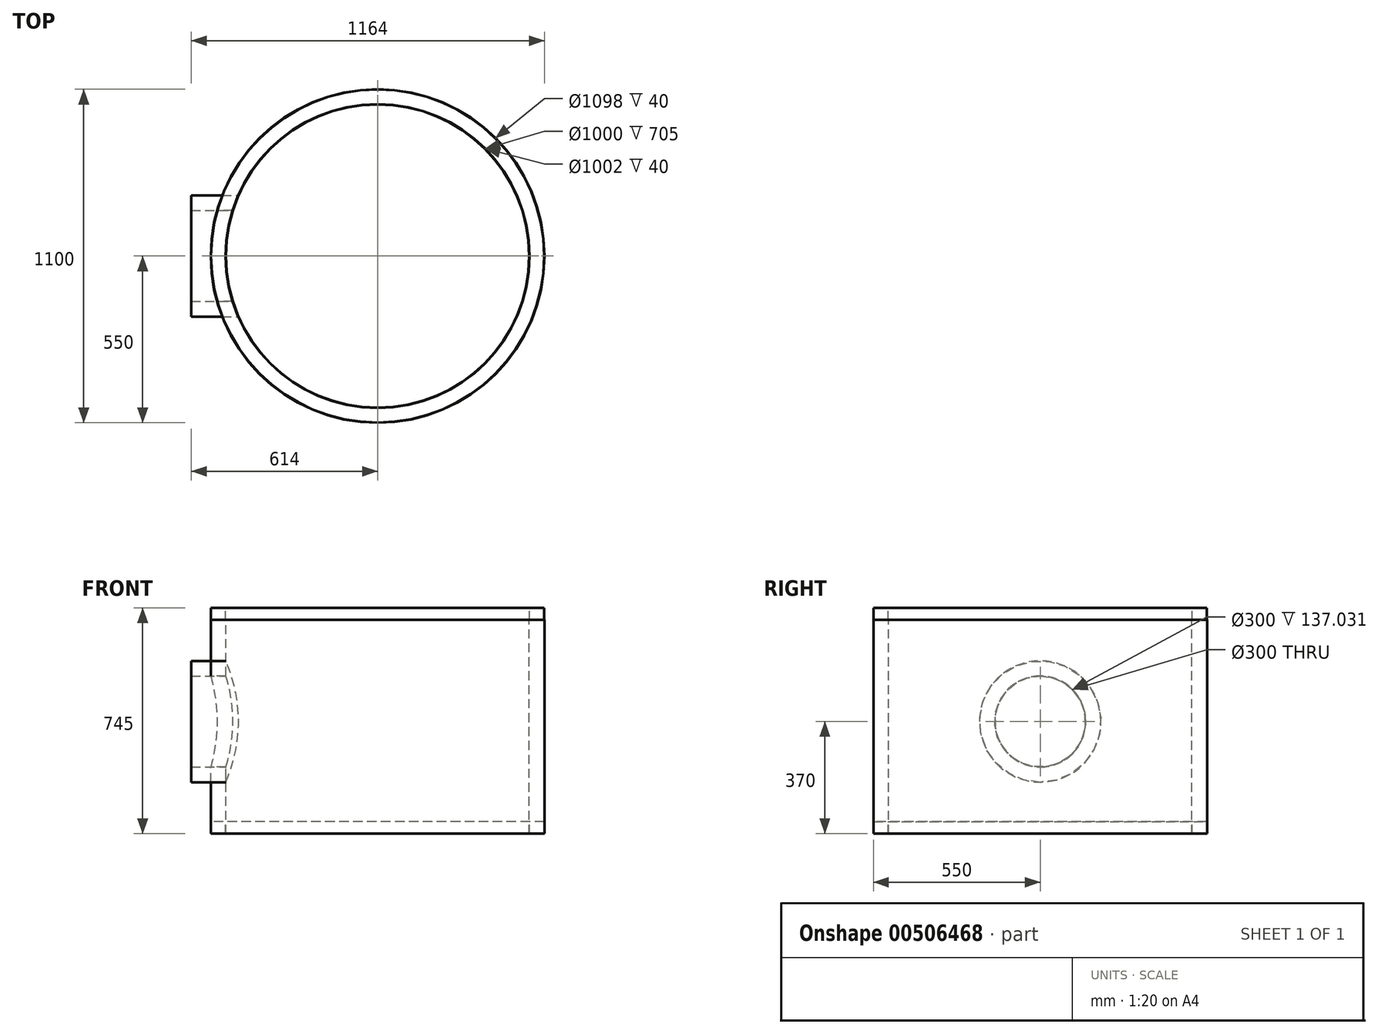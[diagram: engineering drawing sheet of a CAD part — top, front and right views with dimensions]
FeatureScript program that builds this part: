
annotation { "Feature Type Name" : "Feature", "Feature Type Description" : "" }
export const myFeature = defineFeature(function(context is Context, id is Id, definition is map)
    precondition{}
    {
        {
            var Q0;
            Q0=qCreatedBy(makeId("Front.planeOp"),FACE);
            var sketch = newSketch(context, id + "F0", { "sketchPlane" : qUnion([Q0])});
            skLineSegment(sketch, "E0", {"start": v(0, 722.18) * mm, "end": v(0, -793.11) * mm, "construction": true});
            skLineSegment(sketch, "E1", {"start": v(-500, -370) * mm, "end": v(-500, 335) * mm});
            skLineSegment(sketch, "E2", {"start": v(-500, 335) * mm, "end": v(-501, 335) * mm});
            skLineSegment(sketch, "E3", {"start": v(-501, 335) * mm, "end": v(-501, 375) * mm});
            skLineSegment(sketch, "E4", {"start": v(-501, 375) * mm, "end": v(-549, 375) * mm});
            skLineSegment(sketch, "E5", {"start": v(-549, 375) * mm, "end": v(-549, 335) * mm});
            skLineSegment(sketch, "E6", {"start": v(-549, 335) * mm, "end": v(-550, 335) * mm});
            skLineSegment(sketch, "E7", {"start": v(-550, 335) * mm, "end": v(-550, -370) * mm});
            skLineSegment(sketch, "E8", {"start": v(-550, -370) * mm, "end": v(-549, -370) * mm});
            skLineSegment(sketch, "E9", {"start": v(-549, -370) * mm, "end": v(-549, -330) * mm});
            skLineSegment(sketch, "E10", {"start": v(-549, -330) * mm, "end": v(-501, -330) * mm});
            skLineSegment(sketch, "E11", {"start": v(-501, -330) * mm, "end": v(-501, -370) * mm});
            skLineSegment(sketch, "E12", {"start": v(-501, -370) * mm, "end": v(-500, -370) * mm});
            skLineSegment(sketch, "E13", {"start": v(0, 0) * mm, "end": v(-1128, 0) * mm, "construction": true});
            skLineSegment(sketch, "E14", {"start": v(0, -150) * mm, "end": v(-614, -150) * mm});
            skLineSegment(sketch, "E15", {"start": v(-614, -150) * mm, "end": v(-614, -200) * mm});
            skLineSegment(sketch, "E16", {"start": v(-614, -200) * mm, "end": v(0, -200) * mm});
            skLineSegment(sketch, "E17", {"start": v(0, -200) * mm, "end": v(0, -150) * mm});
            skLineSegment(sketch, "E18", {"start": v(-614, -150) * mm, "end": v(-614, 0) * mm});
            skLineSegment(sketch, "E19", {"start": v(-614, 0) * mm, "end": v(-564, 0) * mm});
            skLineSegment(sketch, "E20", {"start": v(-564, 0) * mm, "end": v(-564, -150) * mm});
            skSolve(sketch);
        }
        {
            var Q0;
            {var subQ0=sQuery(id+"F0.wireOp",EDGE,"E2");Q0=makeQuery(id+"F0.imprint","IMPRINT",FACE,{"disambiguationData":[TD([[makeQuery(id+"F0.imprint","IMPRINT",EDGE,{"derivedFrom":subQ0}),1.0]])]});}
            var Q1;
            {var subQ0=sQuery(id+"F0.wireOp",EDGE,"E16");var subQ1=sQuery(id+"F0.wireOp",EDGE,"E1");var subQ2=makeQuery(id+"F0.imprint","INTERSECT",VERTEX,{"derivedFrom":[subQ1,subQ0]});Q1=makeQuery(id+"F0.imprint","IMPRINT",FACE,{"disambiguationData":[TD([[makeQuery(id+"F0.imprint","IMPRINT",EDGE,{"disambiguationData":[TD([[subQ2,-1.0]])],"derivedFrom":subQ1}),1.0]])]});}
            var Q2;
            {var subQ0=sQuery(id+"F0.wireOp",EDGE,"E8");Q2=makeQuery(id+"F0.imprint","IMPRINT",FACE,{"disambiguationData":[TD([[makeQuery(id+"F0.imprint","IMPRINT",EDGE,{"derivedFrom":subQ0}),1.0]])]});}
            var Q3;
            Q3=sQuery(id+"F0.wireOp",EDGE,"E0");
            revolve(context, id + "F1", {"entities" : qUnion([Q0, Q1, Q2]), "axis" : qUnion([Q3]), "revolveType" : RevolveType.FULL});
        }
        {
            var Q0;
            {var subQ0=sQuery(id+"F0.wireOp",EDGE,"E18");Q0=makeQuery(id+"F0.imprint","IMPRINT",FACE,{"disambiguationData":[TD([[makeQuery(id+"F0.imprint","IMPRINT",EDGE,{"derivedFrom":subQ0}),-1.0]])]});}
            var Q1;
            {var subQ0=sQuery(id+"F0.wireOp",EDGE,"E15");Q1=makeQuery(id+"F0.imprint","IMPRINT",FACE,{"disambiguationData":[TD([[makeQuery(id+"F0.imprint","IMPRINT",EDGE,{"derivedFrom":subQ0}),1.0]])]});}
            var Q2;
            {var subQ0=sQuery(id+"F0.wireOp",EDGE,"E16");var subQ1=sQuery(id+"F0.wireOp",EDGE,"E1");var subQ2=makeQuery(id+"F0.imprint","INTERSECT",VERTEX,{"derivedFrom":[subQ1,subQ0]});Q2=makeQuery(id+"F0.imprint","IMPRINT",FACE,{"disambiguationData":[TD([[makeQuery(id+"F0.imprint","IMPRINT",EDGE,{"disambiguationData":[TD([[subQ2,-1.0]])],"derivedFrom":subQ1}),1.0]])]});}
            var Q3;
            {var subQ5=sQuery(id+"F0.wireOp",EDGE,"E17");Q3=makeQuery(id+"F0.imprint","IMPRINT",FACE,{"disambiguationData":[TD([[makeQuery(id+"F0.imprint","IMPRINT",EDGE,{"derivedFrom":subQ5}),1.0]])]});}
            var Q4;
            Q4=sQuery(id+"F0.wireOp",EDGE,"E13");
            revolve(context, id + "F2", {"entities" : qUnion([Q0, Q1, Q2, Q3]), "axis" : qUnion([Q4]), "revolveType" : RevolveType.FULL});
        }
        {
            var Q0;
            Q0=makeQuery(id+"F2.opRevolve","SWEPT_FACE",FACE,{"disambiguationData":[OSD([sQuery(id+"F0.wireOp",EDGE,"E15"),sQuery(id+"F0.wireOp",EDGE,"E18")])]});
            var sketch = newSketch(context, id + "F3", { "sketchPlane" : qUnion([Q0])});
            skCircle(sketch, "E21", {"center": v(0, 0) * mm, "radius": 150 * mm});
            skSolve(sketch);
        }
        {
            var Q0;
            Q0=qSketchRegion(id+"F3",true);
            extrude(context, id + "F4", {"entities" : qUnion([Q0]), "operationType" : NewBodyOperationType.REMOVE, "oppositeDirection" : true, "depth" : 700 * mm, "offsetDistance" : 25 * mm});
        }
        {
            var Q0;
            Q0=makeQuery(id+"F1.opRevolve","SWEPT_FACE",FACE,{"disambiguationData":[OSD([sQuery(id+"F0.wireOp",EDGE,"E4")])]});
            var sketch = newSketch(context, id + "F5", { "sketchPlane" : qUnion([Q0])});
            skCircle(sketch, "E22", {"center": v(0, 0) * mm, "radius": 500 * mm});
            skSolve(sketch);
        }
        {
            var Q0;
            Q0=qSketchRegion(id+"F5",true);
            extrude(context, id + "F6", {"entities" : qUnion([Q0]), "operationType" : NewBodyOperationType.REMOVE, "oppositeDirection" : true, "depth" : 1200 * mm});
        }
    });
